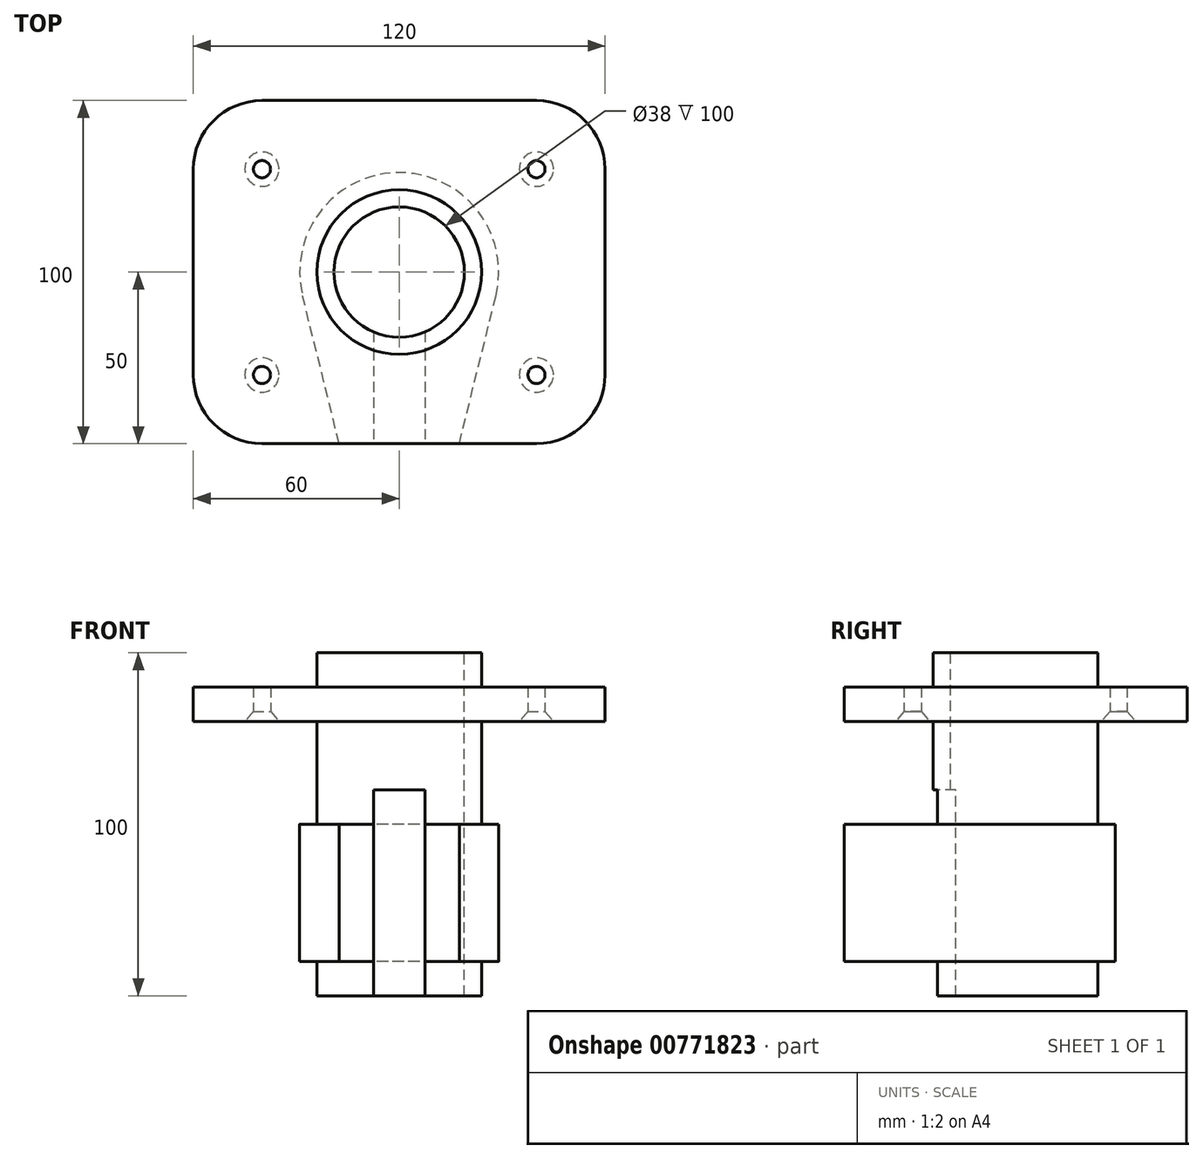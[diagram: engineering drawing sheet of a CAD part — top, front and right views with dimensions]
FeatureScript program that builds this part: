
annotation { "Feature Type Name" : "Feature", "Feature Type Description" : "" }
export const myFeature = defineFeature(function(context is Context, id is Id, definition is map)
    precondition{}
    {
        {
            var Q0;
            Q0=qCreatedBy(makeId("Top.planeOp"),FACE);
            var sketch = newSketch(context, id + "F0", { "sketchPlane" : qUnion([Q0])});
            skCircle(sketch, "E0", {"center": v(0, 0) * mm, "radius": 19 * mm});
            skCircle(sketch, "E1", {"center": v(0, 0) * mm, "radius": 24 * mm});
            skLineSegment(sketch, "E2", {"start": v(0, 0) * mm, "end": v(-7.5, 0) * mm});
            skLineSegment(sketch, "E3", {"start": v(-7.5, 0) * mm, "end": v(-7.5, -50) * mm});
            skLineSegment(sketch, "E4", {"start": v(-7.5, -50) * mm, "end": v(-17.5, -50) * mm});
            skLineSegment(sketch, "E5", {"start": v(-17.5, -50) * mm, "end": v(-28.15, -6.97) * mm});
            skLineSegment(sketch, "E6.MirrorCS", {"start": v(0, 0) * mm, "end": v(7.5, 0) * mm});
            skLineSegment(sketch, "E7.MirrorCS", {"start": v(7.5, 0) * mm, "end": v(7.5, -50) * mm});
            skLineSegment(sketch, "E8.MirrorCS", {"start": v(7.5, -50) * mm, "end": v(17.5, -50) * mm});
            skLineSegment(sketch, "E9.MirrorCS", {"start": v(17.5, -50) * mm, "end": v(28.15, -6.97) * mm});
            skArc(sketch, "E10.trimOffspring", {"start": v(28.15, -6.97) * mm, "mid": v(0, 29) * mm, "end": v(-28.15, -6.97) * mm});
            skSolve(sketch);
        }
        {
            var Q0;
            Q0=qCreatedBy(makeId("Top.planeOp"),FACE);
            cPlane(context, id + "F1", {"entities" : qUnion([Q0]), "cplaneType" : CPlaneType.OFFSET, "offset" : 20 * mm, "width" : 150 * mm, "height" : 150 * mm});
        }
        {
            var Q0;
            Q0=qCreatedBy(id+"F1.planeOp",FACE);
            var sketch = newSketch(context, id + "F2", { "sketchPlane" : qUnion([Q0])});
            skCircle(sketch, "E11", {"center": v(0, 0) * mm, "radius": 19 * mm});
            skLineSegment(sketch, "E12.bottom", {"start": v(-40, -50) * mm, "end": v(40, -50) * mm});
            skLineSegment(sketch, "E12.top", {"start": v(-40, 50) * mm, "end": v(40, 50) * mm});
            skLineSegment(sketch, "E12.left", {"start": v(-60, -30) * mm, "end": v(-60, 30) * mm});
            skLineSegment(sketch, "E12.right", {"start": v(60, -30) * mm, "end": v(60, 30) * mm});
            skPoint(sketch, "E13.visualSharp", {"position": v(-60, 50) * mm});
            skArc(sketch, "E13.filletArc", {"start": v(-40, 50) * mm, "mid": v(-54.14, 44.14) * mm, "end": v(-60, 30) * mm});
            skPoint(sketch, "E14.visualSharp", {"position": v(60, 50) * mm});
            skArc(sketch, "E14.filletArc", {"start": v(60, 30) * mm, "mid": v(54.14, 44.14) * mm, "end": v(40, 50) * mm});
            skPoint(sketch, "E15.visualSharp", {"position": v(60, -50) * mm});
            skArc(sketch, "E15.filletArc", {"start": v(40, -50) * mm, "mid": v(54.14, -44.14) * mm, "end": v(60, -30) * mm});
            skPoint(sketch, "E16.visualSharp", {"position": v(-60, -50) * mm});
            skArc(sketch, "E16.filletArc", {"start": v(-60, -30) * mm, "mid": v(-54.14, -44.14) * mm, "end": v(-40, -50) * mm});
            skSolve(sketch);
        }
        {
            var Q0;
            {var subQ0=sQuery(id+"F0.wireOp",EDGE,"E3");var subQ1=sQuery(id+"F0.wireOp",EDGE,"E0");var subQ2=makeQuery(id+"F0.imprint","INTERSECT",VERTEX,{"derivedFrom":[subQ1,subQ0]});Q0=makeQuery(id+"F0.imprint","IMPRINT",FACE,{"disambiguationData":[TD([[makeQuery(id+"F0.imprint","IMPRINT",EDGE,{"disambiguationData":[TD([[subQ2,1.0]])],"derivedFrom":subQ1}),-1.0]])]});}
            extrude(context, id + "F3", {"entities" : qUnion([Q0]), "oppositeDirection" : true, "depth" : 60 * mm, "offsetDistance" : 25 * mm});
        }
        {
            var Q0;
            {var subQ0=sQuery(id+"F0.wireOp",EDGE,"E4");Q0=makeQuery(id+"F0.imprint","IMPRINT",FACE,{"disambiguationData":[TD([[makeQuery(id+"F0.imprint","IMPRINT",EDGE,{"derivedFrom":subQ0}),-1.0]])]});}
            extrude(context, id + "F4", {"entities" : qUnion([Q0]), "operationType" : NewBodyOperationType.ADD, "oppositeDirection" : true, "depth" : 50 * mm, "offsetDistance" : 25 * mm, "hasSecondDirection" : true, "secondDirectionOppositeDirection" : true, "secondDirectionDepth" : 10 * mm});
        }
        {
            var Q0;
            {var subQ0=sQuery(id+"F0.wireOp",EDGE,"E3");var subQ1=sQuery(id+"F0.wireOp",EDGE,"E0");var subQ2=makeQuery(id+"F0.imprint","INTERSECT",VERTEX,{"derivedFrom":[subQ1,subQ0]});Q0=makeQuery(id+"F0.imprint","IMPRINT",FACE,{"disambiguationData":[TD([[makeQuery(id+"F0.imprint","IMPRINT",EDGE,{"disambiguationData":[TD([[subQ2,1.0]])],"derivedFrom":subQ1}),-1.0]])]});}
            var Q1;
            {var subQ0=sQuery(id+"F0.wireOp",EDGE,"E3");var subQ1=sQuery(id+"F0.wireOp",EDGE,"E0");var subQ2=makeQuery(id+"F0.imprint","INTERSECT",VERTEX,{"derivedFrom":[subQ1,subQ0]});Q1=makeQuery(id+"F0.imprint","IMPRINT",FACE,{"disambiguationData":[TD([[makeQuery(id+"F0.imprint","IMPRINT",EDGE,{"disambiguationData":[TD([[subQ2,-1.0]])],"derivedFrom":subQ1}),-1.0]])]});}
            extrude(context, id + "F5", {"entities" : qUnion([Q0, Q1]), "operationType" : NewBodyOperationType.ADD, "depth" : 40 * mm, "offsetDistance" : 25 * mm});
        }
        {
            var Q0;
            Q0=makeQuery(id+"F2.imprint","IMPRINT",FACE,{"disambiguationData":[TD([[makeQuery(id+"F2.imprint","IMPRINT",EDGE,{"derivedFrom":sQuery(id+"F2.wireOp",EDGE,"E11")}),-1.0]])]});
            extrude(context, id + "F6", {"entities" : qUnion([Q0]), "operationType" : NewBodyOperationType.ADD, "depth" : 10 * mm, "offsetDistance" : 25 * mm});
        }
        {
            var Q0;
            Q0=sQuery(id+"F2.wireOp",VERTEX,"E15.filletArc.center");
            var Q1;
            Q1=sQuery(id+"F2.wireOp",VERTEX,"E14.filletArc.center");
            var Q2;
            Q2=sQuery(id+"F2.wireOp",VERTEX,"E13.filletArc.center");
            var Q3;
            Q3=sQuery(id+"F2.wireOp",VERTEX,"E16.filletArc.center");
            var Q4;
            Q4=makeQuery(id+"F3.opExtrude","SWEPT_BODY",BODY,{"disambiguationData":[OSD([sQuery(id+"F0.wireOp",EDGE,"E0"),sQuery(id+"F0.wireOp",EDGE,"E1"),sQuery(id+"F0.wireOp",EDGE,"E3"),sQuery(id+"F0.wireOp",EDGE,"E7.MirrorCS")])]});
            hole(context, id + "F7", {"style" : HoleStyle.C_SINK, "endStyle" : HoleEndStyle.THROUGH, "oppositeDirection" : true, "holeDiameter" : 5 * mm, "cSinkDiameter" : 10 * mm, "cSinkAngle" : 82 * degree, "majorDiameter" : 5 * mm, "isTappedThrough" : true, "tappedDepth" : 12 * mm, "tapClearance" : 3, "locations" : qUnion([Q0, Q1, Q2, Q3]), "scope" : qUnion([Q4])});
        }
    });
